# Revit family: Nuaire_IfcFanType_MrxboxVm12
name_source: partatom
category: Mechanical Equipment
revit_build: Autodesk Revit 2018 (Build: 20170223_1515(x64)
units: mm (PartAtom-declared; Revit-internal decimal feet)

## family parameters
Always vertical = Yes
Cut with Voids When Loaded = No
OmniClass Number = 23.75.00.00
OmniClass Title = Climate Control (HVAC)
Part Type = Normal
Room Calculation Point = No
Round Connector Dimension = Use Diameter
Shared = No
Work Plane-Based = No

## types (1)
- Nuaire_IfcFanType_MrxboxVm12
    6 Monthly = SFG20 20-03
    Access Clearance Bottom = 199 mm  [stored 0.652887 ft]
    Annually = SFG20 20-03
    Apparent Load = 322 VA
    BMS Links = No
    Battery Supply = No
    Bespoke Timeframe = SFG20 20-03
    CE Approval = Yes
    COBie.Type = Yes
    COBie.Type.Area = 0 m²
    COBie.Type.Category = Centrifugal Fans
    COBie.Type.Color = Black
    COBie.Type.Description = Ceiling Void Moutned MVHR Unit + Bypass
    COBie.Type.DurationUnit = Years
    COBie.Type.Finish = Black EPP Plastic
    COBie.Type.Length = 820 mm  [stored 2.69029 ft]
    COBie.Type.Manufacturer = Nuaire
    COBie.Type.Material = Black EPP Plastic
    COBie.Type.ModelNumber = MRXBOXAB-ECO-VM1
    COBie.Type.ModelReference = MRXBOXAB-ECO-VM1
    COBie.Type.Name = MRXBOXAB-ECO-VM1
    COBie.Type.NominalHeight = 199 mm  [stored 0.652887 ft]
    COBie.Type.NominalLength = 820 mm  [stored 2.69029 ft]
    COBie.Type.NominalWidth = 520 mm  [stored 1.70604 ft]
    COBie.Type.ReplacementCost = 0 $
    COBie.Type.WarrantyDescription = 2 years. First year parts and labour, remaining 1 year parts only.
    COBie.Type.WarrantyDurationLabor = 1
    COBie.Type.WarrantyDurationParts = 2
    COBie.Type.WarrantyDurationUnit = Year
    COBie.Type.WarrantyGuarantorLabor = Nuaire
    COBie.Type.WarrantyGuarantorParts = Nuaire
    Catalogue Pages = http://www.nuaire.info
    Classification.Uniclass.Pr.Description = Centrifugal Fans
    Classification.Uniclass.Pr.Number = Pr_65_67_29_96
    Cost = 0 $
    Daily = SFG20 20-03
    Description = Ceiling Void Moutned MVHR Unit + Bypass
    Duct Connection Height = 60 mm  [stored 0.19685 ft]
    Duct Connection Width = 204 mm  [stored 0.669291 ft]
    Environmental Product Declaration = WEEE, RoHS
    Fire Control Panel Links = No
    Frequency = 50 Hz
    Full Load Current = 1.40 A
    HX Block Condensate Drain Connection Diameter = 32 mm
    Height = 199 mm  [stored 0.652887 ft]
    I&M Manual = https://www.nuaire.co.uk
    IFCExportAs = IfcFanType
    IFCExportType = CENTRIFUGALBACKWARDINCLINEDCURVED
    Length = 820 mm  [stored 2.69029 ft]
    Life Cycle Analysis = 0
    Location of Manufacturer = 51.571856, -3.232638
    Maintenance Required 0 to 300hrs = https://www.nuaire.co.uk
    Maintenance Required 1001 to 2000hrs = https://www.nuaire.co.uk
    Maintenance Required 2001 to 4000hrs = https://www.nuaire.co.uk
    Maintenance Required 301 to 600hrs = https://www.nuaire.co.uk
    Maintenance Required 4001 to 8000hrs = https://www.nuaire.co.uk
    Maintenance Required 601 to 1000hrs = https://www.nuaire.co.uk
    Maintenance Required 8001 to 12000hrs = https://www.nuaire.co.uk
    Manufacturer = Nuaire
    Manufacturer Website = http://www.nuaire.co.uk
    Maximum Ambient Temperature = 40 °C
    Model = MRXBOXAB-ECO-VM1
    Monthly = SFG20 20-03
    Nominal Motor Rating = 0.690 kW
    Nominal Motor Speed (rpm) = 3770
    Number of Connection Poles = 2
    OmniClass Number = 23-33 31 19 13
    OmniClass Title = Whole dwelling fan units
    Operation and Maintenance Manual = https://www.nuaire.co.uk
    Postcode = CF83 1NA
    Power Source = Mains
    Product Literature = http://nuaire.info
    Product Range = MRXBOX
    Quarterly = SFG20 20-03
    Reference Standard = ISO 9001:2015
    Responsible Sourcing of Materials = FSC
    Revit Family Last Revised = 2025-10-20T14:20:00
    Supply Phase = 1
    Telephone Number = +44(0)2920-858-200
    URL = http://www.nuaire.co.uk
    VAT Registration Number = 877308
    Voltage = 230 V
    Weatherproof or Internal Only = Internal
    Weekly = SFG20 20-03
    Weight = 9.00 kg
    Width = 520 mm  [stored 1.70604 ft]

note: [stored X ft] marks values corroborated as IEEE doubles in the binary element streams (Revit-internal decimal feet)

## geometry (parser evidence)
native form markers: Sweep x2
no freeform markers — native parametric forms only
